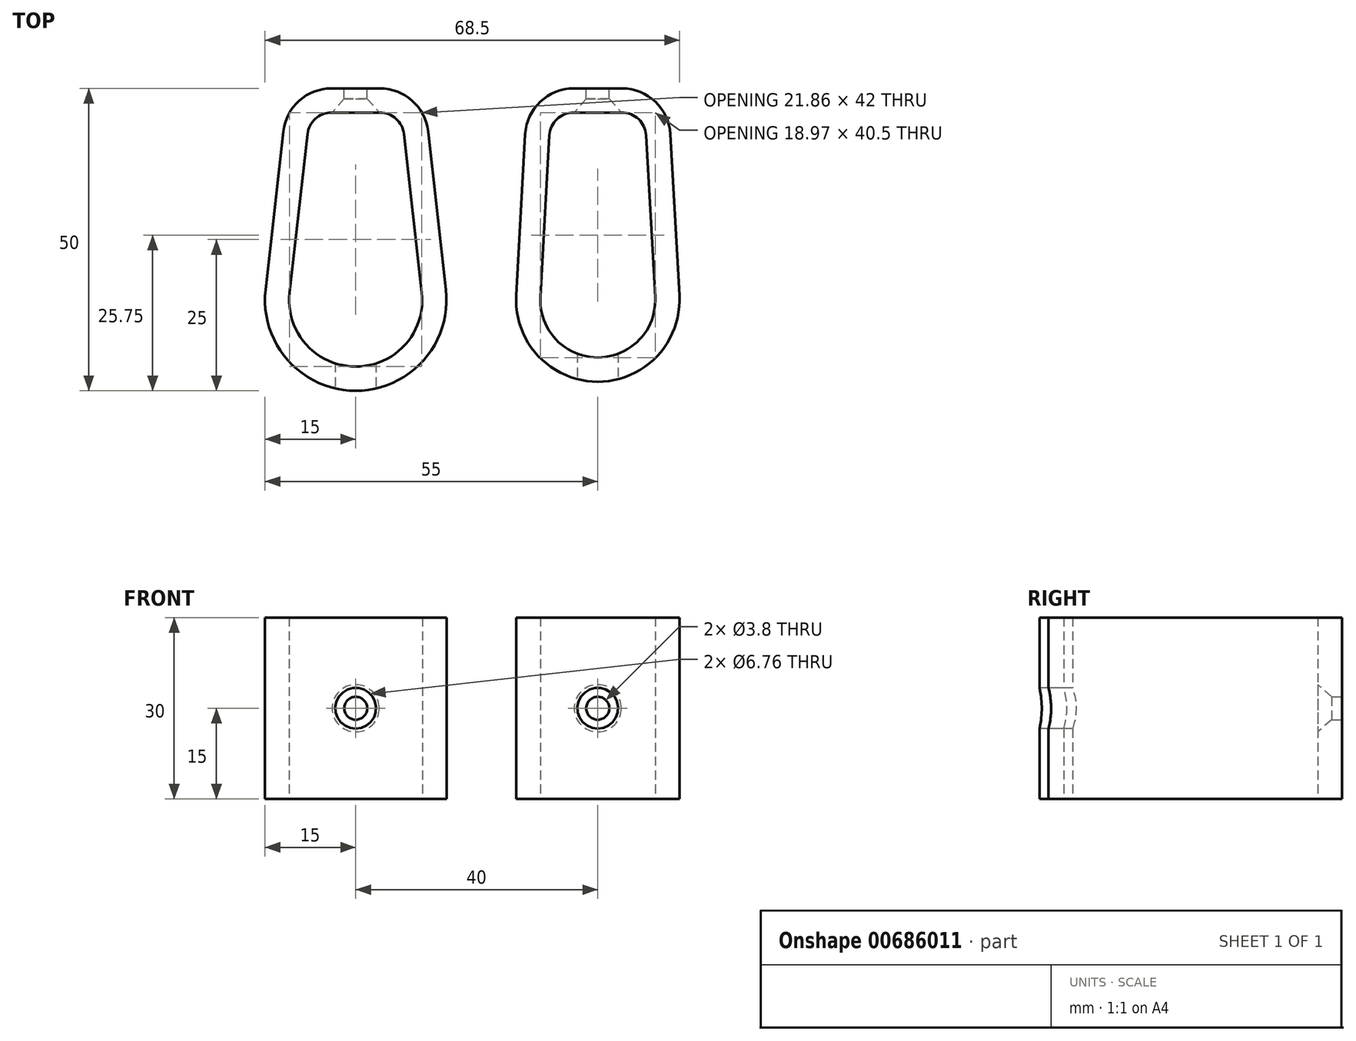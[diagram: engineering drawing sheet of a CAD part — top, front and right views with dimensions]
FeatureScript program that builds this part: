
annotation { "Feature Type Name" : "Feature", "Feature Type Description" : "" }
export const myFeature = defineFeature(function(context is Context, id is Id, definition is map)
    precondition{}
    {
        {
            var Q0;
            Q0=qCreatedBy(makeId("Top.planeOp"),FACE);
            var sketch = newSketch(context, id + "F0", { "sketchPlane" : qUnion([Q0])});
            skArc(sketch, "E0", {"start": v(-30.93, 1.23) * mm, "mid": v(-20, -11) * mm, "end": v(-9.07, 1.23) * mm});
            skArc(sketch, "E1", {"start": v(-5.1, 1.68) * mm, "mid": v(-20, -15) * mm, "end": v(-34.9, 1.68) * mm});
            skLineSegment(sketch, "E2", {"start": v(-24, 31) * mm, "end": v(-16, 31) * mm});
            skLineSegment(sketch, "E3", {"start": v(-16, 35) * mm, "end": v(-24, 35) * mm});
            skArc(sketch, "E4", {"start": v(10.51, 0.53) * mm, "mid": v(20, -9.5) * mm, "end": v(29.49, 0.53) * mm});
            skArc(sketch, "E5", {"start": v(33.48, 0.75) * mm, "mid": v(20, -13.5) * mm, "end": v(6.52, 0.75) * mm});
            skLineSegment(sketch, "E6", {"start": v(16, 35) * mm, "end": v(24, 35) * mm});
            skLineSegment(sketch, "E7", {"start": v(24, 31) * mm, "end": v(16, 31) * mm});
            skLineSegment(sketch, "E8", {"start": v(-20, 11) * mm, "end": v(20, 11) * mm, "construction": true});
            skLineSegment(sketch, "E9", {"start": v(33.48, 0.75) * mm, "end": v(31.99, 27.45) * mm});
            skLineSegment(sketch, "E10", {"start": v(29.49, 0.53) * mm, "end": v(28, 27.22) * mm});
            skLineSegment(sketch, "E11", {"start": v(12, 27.22) * mm, "end": v(10.51, 0.53) * mm});
            skLineSegment(sketch, "E12", {"start": v(6.52, 0.75) * mm, "end": v(8.01, 27.45) * mm});
            skArc(sketch, "E13.filletArc", {"start": v(16, 31) * mm, "mid": v(13.25, 29.9) * mm, "end": v(12, 27.22) * mm});
            skArc(sketch, "E14.filletArc", {"start": v(28, 27.22) * mm, "mid": v(26.75, 29.9) * mm, "end": v(24, 31) * mm});
            skArc(sketch, "E15.filletArc", {"start": v(16, 35) * mm, "mid": v(10.5, 32.81) * mm, "end": v(8.01, 27.45) * mm});
            skArc(sketch, "E16.filletArc", {"start": v(31.99, 27.45) * mm, "mid": v(29.5, 32.81) * mm, "end": v(24, 35) * mm});
            skLineSegment(sketch, "E17", {"start": v(-34.9, 1.68) * mm, "end": v(-31.95, 27.9) * mm});
            skLineSegment(sketch, "E18", {"start": v(-27.97, 27.45) * mm, "end": v(-30.93, 1.23) * mm});
            skLineSegment(sketch, "E19", {"start": v(-12.03, 27.45) * mm, "end": v(-9.07, 1.23) * mm});
            skLineSegment(sketch, "E20", {"start": v(-5.1, 1.68) * mm, "end": v(-8.05, 27.9) * mm});
            skArc(sketch, "E21.filletArc", {"start": v(-12.03, 27.45) * mm, "mid": v(-13.33, 29.98) * mm, "end": v(-16, 31) * mm});
            skArc(sketch, "E22.filletArc", {"start": v(-24, 31) * mm, "mid": v(-26.67, 29.98) * mm, "end": v(-27.97, 27.45) * mm});
            skArc(sketch, "E23.filletArc", {"start": v(-24, 35) * mm, "mid": v(-29.33, 32.97) * mm, "end": v(-31.95, 27.9) * mm});
            skArc(sketch, "E24.filletArc", {"start": v(-8.05, 27.9) * mm, "mid": v(-10.67, 32.97) * mm, "end": v(-16, 35) * mm});
            skPoint(sketch, "E25", {"position": v(0, 11) * mm});
            skSolve(sketch);
        }
        {
            var Q0;
            Q0 = qSketchRegion(id + "F0", true);
            extrude(context, id + "F1", {"entities" : qUnion([Q0]), "depth" : 30 * mm, "offsetDistance" : 25 * mm});
        }
        {
            var Q0;
            Q0=makeQuery(id+"F1.opExtrude","SWEPT_FACE",FACE,{"disambiguationData":[OSD([sQuery(id+"F0.wireOp",EDGE,"E7")])]});
            var sketch = newSketch(context, id + "F2", { "sketchPlane" : qUnion([Q0])});
            skLineSegment(sketch, "E26", {"start": v(20, 0) * mm, "end": v(20, 30) * mm, "construction": true});
            skPoint(sketch, "E27", {"position": v(20, 15) * mm});
            skLineSegment(sketch, "E28", {"start": v(-20, 30) * mm, "end": v(-20, 0) * mm, "construction": true});
            skPoint(sketch, "E29", {"position": v(-20, 15) * mm});
            skSolve(sketch);
        }
        {
            var Q0;
            Q0=sQuery(id+"F2.wireOp",VERTEX,"E27");
            var Q1;
            Q1=sQuery(id+"F2.wireOp",VERTEX,"E29");
            var Q2;
            Q2=makeQuery(id+"F1.opExtrude","SWEPT_BODY",BODY,{"disambiguationData":[OSD([sQuery(id+"F0.wireOp",EDGE,"E0"),sQuery(id+"F0.wireOp",EDGE,"E1"),sQuery(id+"F0.wireOp",EDGE,"679cd62f-0249-49c1-ac3b-d094a6b0fa66"),sQuery(id+"F0.wireOp",EDGE,"7595df1e-b490-476d-9e06-a6d21fcdf787"),sQuery(id+"F0.wireOp",EDGE,"fbd421c0-0e62-499f-aed2-e8e9c44bf252"),sQuery(id+"F0.wireOp",EDGE,"964bbc38-4d97-4ab1-bfb3-b2ee0afa86cb"),sQuery(id+"F0.wireOp",EDGE,"E2"),sQuery(id+"F0.wireOp",EDGE,"gUHBpvEg-dOw2-h8lk-j9jS-JmE95lL3a2xa"),sQuery(id+"F0.wireOp",EDGE,"E3"),sQuery(id+"F0.wireOp",EDGE,"lt6LSE3t-yrWu-z6c1-PSgp-gui3N2zHpmQQ"),sQuery(id+"F0.wireOp",EDGE,"U7GRsJbn-LpbN-mfBc-i6ME-H558zfQFdWCx"),sQuery(id+"F0.wireOp",EDGE,"xfTzrw4F-iqcC-v5Gf-Ungl-jl36YI01kaYe")])]});
            var Q3;
            Q3=makeQuery(id+"F1.opExtrude","SWEPT_BODY",BODY,{"disambiguationData":[OSD([sQuery(id+"F0.wireOp",EDGE,"E4"),sQuery(id+"F0.wireOp",EDGE,"E5"),sQuery(id+"F0.wireOp",EDGE,"ac801f46-a0f2-409b-97da-bcc5bc8a6dfa"),sQuery(id+"F0.wireOp",EDGE,"fe40f5e1-eaff-4ef2-83c0-8f56ba903066"),sQuery(id+"F0.wireOp",EDGE,"3a1c6aa0-ddb5-4744-a3ee-d758a3f80ac6"),sQuery(id+"F0.wireOp",EDGE,"cc9d94e0-b2ed-4136-9c73-1e4e1c83d001"),sQuery(id+"F0.wireOp",EDGE,"E6"),sQuery(id+"F0.wireOp",EDGE,"H3j3XxsU-0oP9-jxR4-JiPk-2g5Toc6r6rqi"),sQuery(id+"F0.wireOp",EDGE,"E7"),sQuery(id+"F0.wireOp",EDGE,"Xv67DJQn-a1VS-GcKj-8JL4-IJMZVQ8XzSeo"),sQuery(id+"F0.wireOp",EDGE,"fAEX9h20-6M4C-l7Zx-E8ny-8lXGCg99QZGS"),sQuery(id+"F0.wireOp",EDGE,"9hs4je5j-T6Ny-E78E-xVrC-XXzAQB1o8C2x")])]});
            hole(context, id + "F3", {"style" : HoleStyle.C_SINK, "endStyle" : HoleEndStyle.THROUGH, "standardTappedOrClearance" : lookupTablePath({ "fit" : "Free", "standard" : "ANSI", "size" : "#6", "type" : "Clearance" }), "standardBlindInLast" : lookupTablePath({ "fit" : "Free", "standard" : "ANSI", "engagement" : "75%", "pitch" : "32 tpi", "size" : "#6", "type" : "Clearance & tapped" }), "holeDiameter" : 3.8 * mm, "cSinkDiameter" : 7.8 * mm, "cSinkAngle" : 82 * degree, "majorDiameter" : 5 * mm, "isTappedThrough" : true, "tappedDepth" : 12 * mm, "tapClearance" : 3, "locations" : qUnion([Q0, Q1]), "scope" : qUnion([Q2, Q3]), "startStyle" : HoleStartStyle.PART});
        }
        {
            var Q0;
            Q0=sQuery(id+"F2.wireOp",VERTEX,"E29");
            var Q1;
            Q1=sQuery(id+"F2.wireOp",VERTEX,"E27");
            var Q2;
            Q2=makeQuery(id+"F1.opExtrude","SWEPT_BODY",BODY,{"disambiguationData":[OSD([sQuery(id+"F0.wireOp",EDGE,"E0"),sQuery(id+"F0.wireOp",EDGE,"E1"),sQuery(id+"F0.wireOp",EDGE,"E2"),sQuery(id+"F0.wireOp",EDGE,"E3"),sQuery(id+"F0.wireOp",EDGE,"E17"),sQuery(id+"F0.wireOp",EDGE,"E18"),sQuery(id+"F0.wireOp",EDGE,"E19"),sQuery(id+"F0.wireOp",EDGE,"E20"),sQuery(id+"F0.wireOp",EDGE,"E21.filletArc"),sQuery(id+"F0.wireOp",EDGE,"E22.filletArc"),sQuery(id+"F0.wireOp",EDGE,"E23.filletArc"),sQuery(id+"F0.wireOp",EDGE,"E24.filletArc")])]});
            var Q3;
            Q3=makeQuery(id+"F1.opExtrude","SWEPT_BODY",BODY,{"disambiguationData":[OSD([sQuery(id+"F0.wireOp",EDGE,"E4"),sQuery(id+"F0.wireOp",EDGE,"E5"),sQuery(id+"F0.wireOp",EDGE,"E6"),sQuery(id+"F0.wireOp",EDGE,"E7"),sQuery(id+"F0.wireOp",EDGE,"E9"),sQuery(id+"F0.wireOp",EDGE,"E10"),sQuery(id+"F0.wireOp",EDGE,"E11"),sQuery(id+"F0.wireOp",EDGE,"E12"),sQuery(id+"F0.wireOp",EDGE,"E13.filletArc"),sQuery(id+"F0.wireOp",EDGE,"E14.filletArc"),sQuery(id+"F0.wireOp",EDGE,"E15.filletArc"),sQuery(id+"F0.wireOp",EDGE,"E16.filletArc")])]});
            hole(context, id + "F4", {"style" : HoleStyle.SIMPLE, "endStyle" : HoleEndStyle.THROUGH, "oppositeDirection" : true, "standardTappedOrClearance" : lookupTablePath({ "fit" : "Free", "standard" : "ANSI", "size" : "1/4", "type" : "Clearance" }), "standardBlindInLast" : lookupTablePath({ "fit" : "Free", "standard" : "ANSI", "engagement" : "75%", "pitch" : "20 tpi", "size" : "1/4", "type" : "Clearance & tapped" }), "holeDiameter" : 6.76 * mm, "majorDiameter" : 5 * mm, "isTappedThrough" : true, "tappedDepth" : 12 * mm, "tapClearance" : 3, "locations" : qUnion([Q0, Q1]), "scope" : qUnion([Q2, Q3]), "startStyle" : HoleStartStyle.PART});
        }
    });
